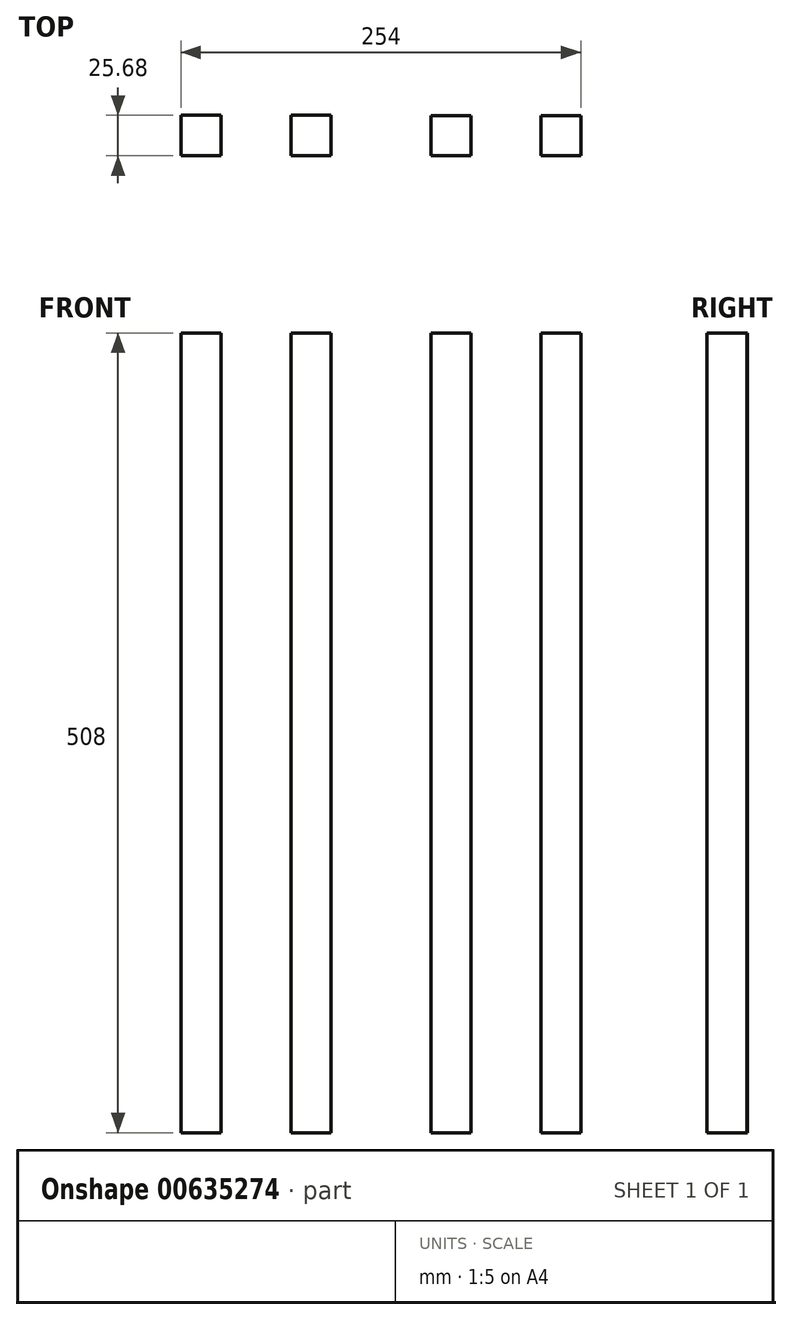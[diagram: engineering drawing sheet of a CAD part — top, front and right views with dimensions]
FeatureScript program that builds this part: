
annotation { "Feature Type Name" : "Feature", "Feature Type Description" : "" }
export const myFeature = defineFeature(function(context is Context, id is Id, definition is map)
    precondition{}
    {
        {
            assignVariable(context, id + "F0", {"name" : "beamHeighth", "anyValue" : 508 * mm});
        }
        {
            var Q0;
            Q0=qCreatedBy(makeId("Top.planeOp"),FACE);
            var sketch = newSketch(context, id + "F1", { "sketchPlane" : qUnion([Q0])});
            skLineSegment(sketch, "E0.bottom", {"start": v(0, 0) * mm, "end": v(25.4, 0) * mm});
            skLineSegment(sketch, "E0.top", {"start": v(0, 25.4) * mm, "end": v(25.4, 25.4) * mm});
            skLineSegment(sketch, "E0.left", {"start": v(0, 0) * mm, "end": v(0, 25.4) * mm});
            skLineSegment(sketch, "E0.right", {"start": v(25.4, 0) * mm, "end": v(25.4, 25.4) * mm});
            skLineSegment(sketch, "E1.bottom", {"start": v(69.85, 0) * mm, "end": v(95.25, 0) * mm});
            skLineSegment(sketch, "E1.top", {"start": v(69.85, 25.4) * mm, "end": v(95.25, 25.4) * mm});
            skLineSegment(sketch, "E1.left", {"start": v(69.85, 0) * mm, "end": v(69.85, 25.4) * mm});
            skLineSegment(sketch, "E1.right", {"start": v(95.25, 0) * mm, "end": v(95.25, 25.4) * mm});
            skLineSegment(sketch, "E2.bottom", {"start": v(-63.5, 0) * mm, "end": v(-88.9, 0) * mm});
            skLineSegment(sketch, "E2.top", {"start": v(-63.5, 25.68) * mm, "end": v(-88.9, 25.68) * mm});
            skLineSegment(sketch, "E2.left", {"start": v(-63.5, 0) * mm, "end": v(-63.5, 25.68) * mm});
            skLineSegment(sketch, "E2.right", {"start": v(-88.9, 0) * mm, "end": v(-88.9, 25.68) * mm});
            skLineSegment(sketch, "E3.bottom", {"start": v(-133.35, 0) * mm, "end": v(-158.75, 0) * mm});
            skLineSegment(sketch, "E3.top", {"start": v(-133.35, 25.68) * mm, "end": v(-158.75, 25.68) * mm});
            skLineSegment(sketch, "E3.left", {"start": v(-133.35, 0) * mm, "end": v(-133.35, 25.68) * mm});
            skLineSegment(sketch, "E3.right", {"start": v(-158.75, 0) * mm, "end": v(-158.75, 25.68) * mm});
            skSolve(sketch);
        }
        {
            var Q0;
            Q0 = qSketchRegion(id + "F1", true);
            extrude(context, id + "F2", {"entities" : qUnion([Q0]), "depth" : getVariable(context, 'beamHeighth'), "offsetDistance" : 25 * mm});
        }
    });
